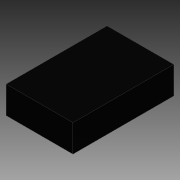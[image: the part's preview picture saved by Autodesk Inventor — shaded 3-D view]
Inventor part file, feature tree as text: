
AUTODESK INVENTOR PART (.ipt)
format: ipt  version: 2015 (Build 190159000, 159)  size: 69,632 bytes
history: native  units: in
note: dims shown in document units (in); Inventor stores cm internally (conversion verified against a paired STEP export)
features: extrude x1, sketch x1
ambient origin geometry x8: Origin, YZ Plane, XZ Plane, XY Plane, X Axis, Y Axis, Z Axis, Center Point
bodies: Solid1 (feature_tree)
feature tree (2):
  extrude  "Extrusion1"  Depth=1.225in
  sketch  "Sketch1"  dims[d0=1.85in d1=1.225in d2=0.5in d3=0.0in]
